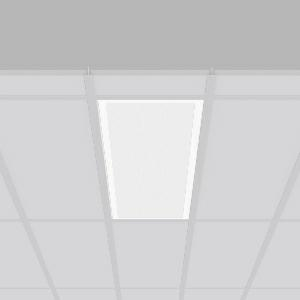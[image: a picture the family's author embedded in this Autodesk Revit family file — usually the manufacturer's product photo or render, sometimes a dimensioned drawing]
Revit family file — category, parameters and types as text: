
# Revit family: sidelite_eco_312368_002_1_76_b69d
name_source: partatom
category: Lighting Fixtures
units: mm (PartAtom-declared; Revit-internal decimal feet)

## family parameters
Cut with Voids When Loaded = No
Host = Face
Light Source = No
Part Type = Normal
Room Calculation Point = No
Round Connector Dimension = Use Diameter
Shared = No

## types (1)
- MultiLumen 1 (1 x LED Modul 840, 3500 lm, 4000)
    Apparent Load = 29 VA
    CIE Flux Codes = 64 88 97 100 100
    Color Rendering = 80
    Color Temperature = 4000
    Default Elevation = 1800 mm
    Description = Series: SIDELITE ECO
Highly economical recessed luminaire with progressive LED technology. Frame made of aluminium, powder-coated. Diffuser plastic microprismatic. Lightguide and diffuser made of non-yellowing plastic (PMMA). Lateral light emission (RZB SIDELITE technology) for homogeneous light distribution. External driver. External driver with simple plug-in locking system and extended converter connecting cable to luminaire (1.90 m). MultiLumen: 4 steps adjustable luminous flux. Factory setting is the lowest offered step. Luminaire can be used with accessories (to be ordered separately) as recessed or surface mounting luminaire. Perfect for office areas (RUG < 19) and environments with computer screens in accordance with EN 12464-1. Qualified for use in the food and drink industry. 
Colour: white
Length: 1245 mm
Width: 308 mm
Cut-out length: 1233 mm
Cut-out width: 296 mm
Recess height: 160 mm
Luminaire: recess height: 38 mm
Lamp: LED
Socket: without socket
Colour temperature: 4000K
Colour rendering index (CRI): 80
System power: 29 W
Rated luminous flux: 3500 lm
Luminous efficiency: 121 lm/W
System power 2: 33 W
Rated luminous flux 2: 3850 lm
Luminous efficiency 2: 117 lm/W
System power 3: 35 W
Rated luminous flux 3: 4050 lm
Luminous efficiency 3: 116 lm/W
System power 4: 38 W
Rated luminous flux 4: 4400 lm
Luminous efficiency 4: 116 lm/W
Control gear: Converter, dimmable, DALI
Protection class: II
Type of protection: IP 40
    Height = 0 mm  [stored 0 ft]
    Lamp = 1 x LED Modul 840
    Lamp Light Flux = 3500 lm
    Lamp count = 1
    Length = 1245 mm
    Lifetime = 50000 h
    Luminous efficacy = 121 lm/W
    Manufacturer = RZB
    ModVariant = No
    Model = 312368.002.1.76
    Mounting Place = Ceiling
    Mounting Type = Recessed
    Number of Poles = 1
    OnlyDefault = Yes
    Power Factor = 1
    Product Name = SIDELITE ECO
    Product group = Recessed modular luminaires
    ProductGroupID = 406
    Protection Class = Protection class II
    Protection Degree = IP 20
    RLX_Detail_Level = 1
    RLX_Emergency_Light_Flux = 0 lm
    RLX_Emergency_Type = 0
    RLX_Emergency_Type_DB = No
    RlxData = <blob elided: 35921 chars, md5=f8586051>
    Socket = socket
    Standby Power = 0 W
    System Light Flux = 3500 lm
    System Power = 29 W
    Type Comments = MultiLumen 1
    Type Image = 312368.002.jpg
    URL = http://relux.com
    VarID = multilumen_1
    Voltage = 230 V
    Voltage Range = 220-240 V
    Weight = 0.00 kg
    Width = 308 mm

note: [stored X ft] marks values corroborated as IEEE doubles in the binary element streams (Revit-internal decimal feet)

## geometry (parser evidence)
native form markers: Blend x4, Sweep x11
no freeform markers — native parametric forms only
